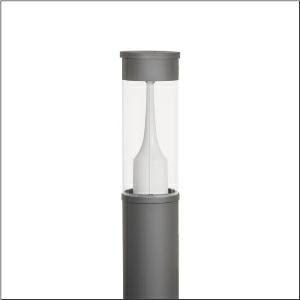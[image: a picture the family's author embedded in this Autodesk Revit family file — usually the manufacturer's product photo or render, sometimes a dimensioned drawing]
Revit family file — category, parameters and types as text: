
# Revit family: city-light_260_iq___p1_0a_5xa5295bf14h_d7c3
name_source: partatom
category: Lighting Fixtures
units: mm (PartAtom-declared; Revit-internal decimal feet)

## family parameters
Cut with Voids When Loaded = No
Host = Face
Light Source = No
Part Type = Normal
Room Calculation Point = No
Round Connector Dimension = Use Diameter
Shared = No

## types (1)
- --- (1 x LED, 1510 lm, 12.9 W, 2200K)
    Apparent Load = 13 VA
    CIE Flux Codes = 32 61 90 93 100
    Color Rendering = 70
    Color Temperature = 2200K
    Default Elevation = 1800 mm
    Description = City-Light 260 iQ, light pillar, Module 540 iQ-SR, primary light control with 3 zone facetted reflector, of plastic, silver coated, highly specular, structured, primary optical cover: cover, of PMMA, transparent, partly coated, light distribution: P1.0a, primary light characteristic: strongly asymmetric, LED, High Power LED, rated luminous flux: 1.510lm, luminous efficacy: 117lm/W, light colour: 722, colour temperature: 2200K, control gear: ECG iQ, control: presetting dimming logarithmic, Street-Remote, Auto-Match, Temp-Guard, Lumen-Switch, Night-Set, Smart-Wire, Light-Fading, Desk-Remote (wireless, voltage-free reading and setting of iQ features in the workshop via application-optimized NFC function/RFID function), optimised constant luminous flux control (CLO 2.0), with terminal, 6-pole, max. 2.5mm², mains connection: 230..240V, AC, 50/60Hz, start of lifetime: 13W, end of service life: 13W, reduction: 6W, luminaire housing, cylindrical, of extruded aluminium section, coated, Siteco® metallic grey (DB 702S), length: 2.600mm, diameter: 200mm, Module 540 iQ-SR, traffic white (RAL 9016), equipment: standard, protection rating (complete): IP65, insulation class (complete): insulation class II (safety insulation), certification: CE, ENEC, VDE, packaging unit: 1 piece

Light Distribution: P1.0a
    Height = 500 mm
    Lamp = 1 x LED
    Lamp Light Flux = 1510 lm
    Lamp Power = 12.9 W
    Lamp count = 1
    Length = 200 mm  [stored 0.656168 ft]
    Luminous efficacy = 117 lm/W
    Manufacturer = Siteco
    ModVariant = No
    Model = 5XA5295BF14H
    Mounting Place = Floor
    Mounting Type = Freestanding
    Number of Poles = 1
    OnlyDefault = Yes
    Power Factor = 1
    Product Name = City-Light 260 iQ | P1.0a
    Product group = light pillar
    ProductGroupID = 1303
    Protection Class = Protection class II
    Protection Degree = IP 65
    RLX_Detail_Level = 1
    RLX_Emergency_Light_Flux = 0 lm
    RLX_Emergency_Type = 0
    RLX_Emergency_Type_DB = No
    RlxData = <blob elided: 52777 chars, md5=191d81ff>
    Socket = socket
    Standby Power = 0 W
    System Light Flux = 1510 lm
    System Power = 13 W
    Type Comments = factory setting: luminous flux: 100 % | dim-lin: 254 | 516 mA
    Type Image = l_1006918.jpg
    URL = http://relux.com
    VarID = @adj_109705
    Voltage = 0 V
    Weight = 0.00 kg
    Width = 0 mm  [stored 0 ft]

note: [stored X ft] marks values corroborated as IEEE doubles in the binary element streams (Revit-internal decimal feet)

## geometry (parser evidence)
native form markers: Blend x4, Sweep x10
no freeform markers — native parametric forms only
